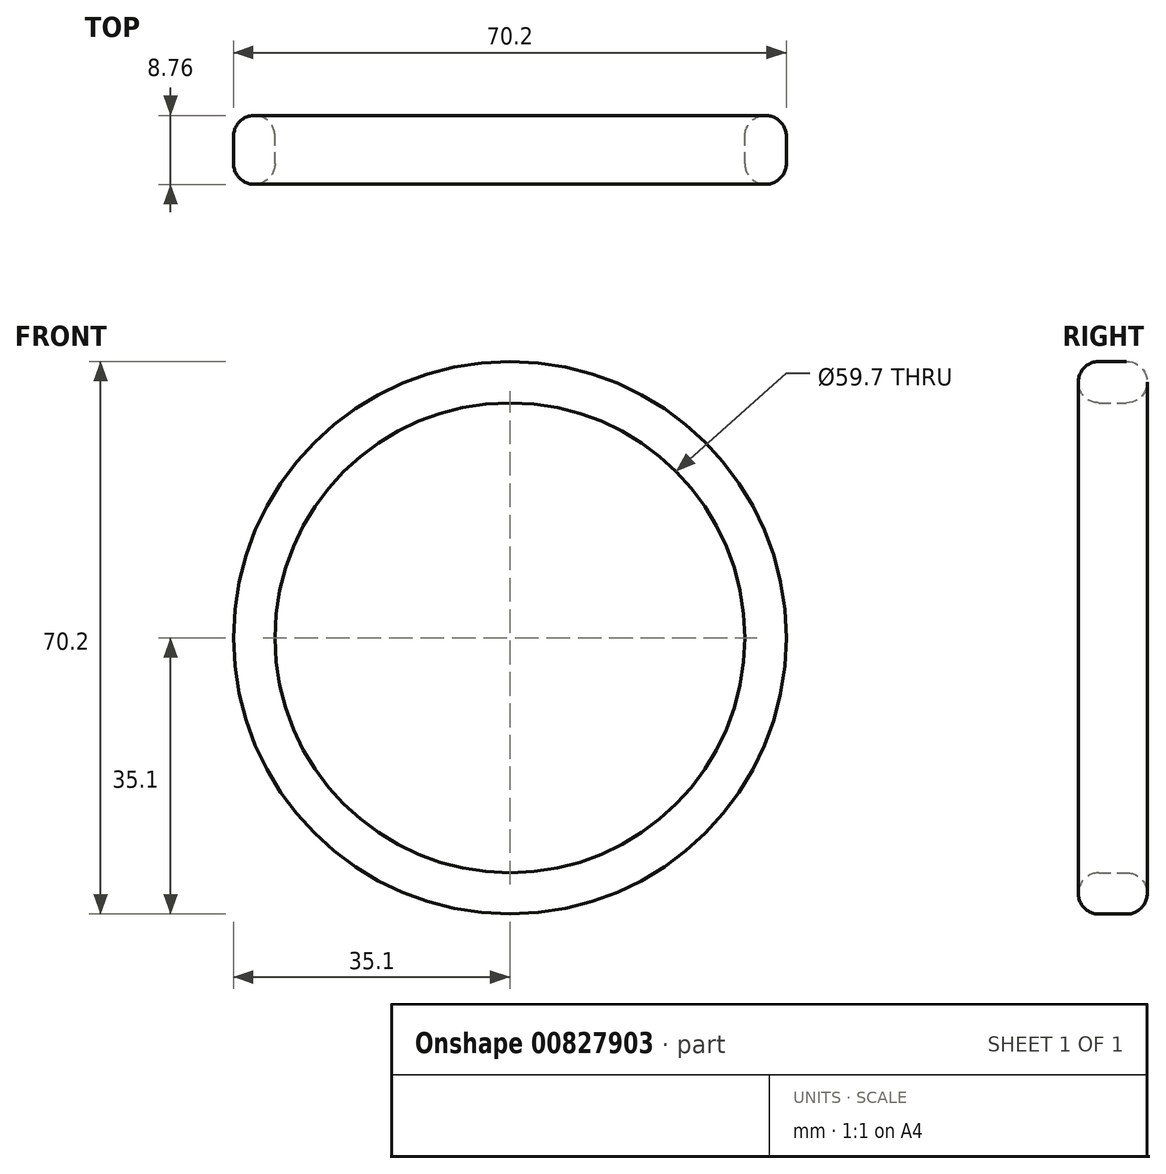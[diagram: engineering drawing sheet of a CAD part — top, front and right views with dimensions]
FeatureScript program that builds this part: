
annotation { "Feature Type Name" : "Feature", "Feature Type Description" : "" }
export const myFeature = defineFeature(function(context is Context, id is Id, definition is map)
    precondition{}
    {
        {
            var Q0;
            Q0=qCreatedBy(makeId("Right.planeOp"),FACE);
            var sketch = newSketch(context, id + "F0", { "sketchPlane" : qUnion([Q0])});
            skLineSegment(sketch, "E0.bottom", {"start": v(1.75, 35.1) * mm, "end": v(-1.75, 35.1) * mm});
            skLineSegment(sketch, "E0.top", {"start": v(1.75, 29.85) * mm, "end": v(-1.75, 29.85) * mm});
            skPoint(sketch, "E0.middle", {"position": v(0, 32.48) * mm});
            skArc(sketch, "E1", {"start": v(1.75, 29.85) * mm, "mid": v(4.38, 32.48) * mm, "end": v(1.75, 35.1) * mm});
            skArc(sketch, "E2", {"start": v(-1.75, 35.1) * mm, "mid": v(-4.38, 32.48) * mm, "end": v(-1.75, 29.85) * mm});
            skLineSegment(sketch, "E3", {"start": v(0, 0) * mm, "end": v(-9.37, 0) * mm, "construction": true});
            skLineSegment(sketch, "E4", {"start": v(-4.38, 32.48) * mm, "end": v(4.37, 32.48) * mm, "construction": true});
            skSolve(sketch);
        }
        {
            var Q0;
            Q0 = qSketchRegion(id + "F0", true);
            var Q1;
            Q1=sQuery(id+"F0.wireOp",EDGE,"E3");
            revolve(context, id + "F1", {"surfaceOperationType" : NewSurfaceOperationType.NEW, "entities" : qUnion([Q0]), "axis" : qUnion([Q1]), "revolveType" : RevolveType.FULL});
        }
        {
            var Q0;
            Q0=qCreatedBy(makeId("Right.planeOp"),FACE);
            var sketch = newSketch(context, id + "F2", { "sketchPlane" : qUnion([Q0])});
            skLineSegment(sketch, "E5", {"start": v(0.72, 0) * mm, "end": v(-12.76, 0) * mm, "construction": true});
            skArc(sketch, "E6", {"start": v(1.75, 29.85) * mm, "mid": v(3.5, 30.51) * mm, "end": v(4.36, 32.17) * mm});
            skArc(sketch, "E7", {"start": v(4.38, -32.48) * mm, "mid": v(3.6, -30.62) * mm, "end": v(1.75, -29.85) * mm});
            skArc(sketch, "E8", {"start": v(-4.38, 32.48) * mm, "mid": v(-3.6, 30.62) * mm, "end": v(-1.75, 29.85) * mm});
            skLineSegment(sketch, "E9", {"start": v(-1.75, 29.85) * mm, "end": v(1.75, 29.85) * mm});
            skLineSegment(sketch, "E10", {"start": v(-4.38, 32.48) * mm, "end": v(-4.38, -32.48) * mm, "construction": true});
            skLineSegment(sketch, "E11", {"start": v(4.38, 32.48) * mm, "end": v(4.38, -32.48) * mm, "construction": true});
            skLineSegment(sketch, "E12", {"start": v(-4.38, 32.48) * mm, "end": v(-4.38, 27.17) * mm});
            skLineSegment(sketch, "E13", {"start": v(-4.38, 27.17) * mm, "end": v(4.38, 27.17) * mm});
            skLineSegment(sketch, "E14", {"start": v(4.37, 27.17) * mm, "end": v(4.36, 32.17) * mm});
            skSolve(sketch);
        }
        {
            var Q0;
            Q0 = qSketchRegion(id + "F2", true);
            var Q1;
            Q1=sQuery(id+"F2.wireOp",EDGE,"E5");
            revolve(context, id + "F3", {"surfaceOperationType" : NewSurfaceOperationType.NEW, "entities" : qUnion([Q0]), "axis" : qUnion([Q1]), "revolveType" : RevolveType.FULL});
        }
        {
            var Q0;
            Q0=qCreatedBy(makeId("Front.planeOp"),FACE);
            var sketch = newSketch(context, id + "F4", { "sketchPlane" : qUnion([Q0])});
            skArc(sketch, "E15", {"start": v(-1.28, 1.5) * mm, "mid": v(-1.95, -0.29) * mm, "end": v(-0.8, -1.8) * mm});
            skLineSegment(sketch, "E16", {"start": v(-1.28, 1.5) * mm, "end": v(1.28, 1.5) * mm});
            skArc(sketch, "E17", {"start": v(0.8, -6.95) * mm, "mid": v(2.41, -6.57) * mm, "end": v(3.89, -5.82) * mm});
            skLineSegment(sketch, "E18", {"start": v(-0.8, -1.8) * mm, "end": v(-0.8, -6.95) * mm});
            skLineSegment(sketch, "E19", {"start": v(-0.8, -1.8) * mm, "end": v(0.8, -1.8) * mm, "construction": true});
            skLineSegment(sketch, "E20", {"start": v(0.8, -1.8) * mm, "end": v(0.8, -6.95) * mm});
            skArc(sketch, "E21.trimOffspring", {"start": v(0.8, -1.8) * mm, "mid": v(1.95, -0.29) * mm, "end": v(1.28, 1.5) * mm});
            skCircle(sketch, "E22.0", {"center": v(0, 0) * mm, "radius": 27.17 * mm, "construction": true});
            skLineSegment(sketch, "E23", {"start": v(0, 0) * mm, "end": v(13.58, 23.53) * mm, "construction": true});
            skLineSegment(sketch, "E24", {"start": v(13.58, 23.53) * mm, "end": v(-13.58, 23.53) * mm, "construction": true});
            skLineSegment(sketch, "E25", {"start": v(-13.58, 23.53) * mm, "end": v(0, 0) * mm, "construction": true});
            skArc(sketch, "E26", {"start": v(-3.5, 6.06) * mm, "mid": v(-3.3, 6.18) * mm, "end": v(-3.11, 6.3) * mm});
            skArc(sketch, "E27", {"start": v(3.1, 6.28) * mm, "mid": v(8.8, 14.9) * mm, "end": v(10.36, 25.11) * mm});
            skArc(sketch, "E28", {"start": v(3.5, 6.06) * mm, "mid": v(3.3, 6.18) * mm, "end": v(3.11, 6.3) * mm});
            skArc(sketch, "E29", {"start": v(-3.1, 6.28) * mm, "mid": v(-8.8, 14.9) * mm, "end": v(-10.36, 25.11) * mm});
            skArc(sketch, "E30", {"start": v(6.38, 26.4) * mm, "mid": v(8.4, 25.84) * mm, "end": v(10.36, 25.11) * mm});
            skArc(sketch, "E31", {"start": v(-6.38, 26.4) * mm, "mid": v(-8.4, 25.84) * mm, "end": v(-10.36, 25.11) * mm});
            skArc(sketch, "E32.1.0", {"start": v(-7, 0) * mm, "mid": v(-7, -0.22) * mm, "end": v(-7, -0.45) * mm});
            skArc(sketch, "E32.1.1", {"start": v(-3.89, -5.82) * mm, "mid": v(-8.5, -15.08) * mm, "end": v(-16.57, -21.53) * mm});
            skArc(sketch, "E32.1.2", {"start": v(-3.5, -6.06) * mm, "mid": v(-3.7, -5.95) * mm, "end": v(-3.9, -5.84) * mm});
            skArc(sketch, "E32.1.3", {"start": v(-6.99, -0.45) * mm, "mid": v(-17.3, 0.18) * mm, "end": v(-26.93, -3.58) * mm});
            skArc(sketch, "E32.1.4", {"start": v(-19.68, -18.73) * mm, "mid": v(-18.18, -20.2) * mm, "end": v(-16.57, -21.53) * mm});
            skArc(sketch, "E32.1.5", {"start": v(-26.06, -7.68) * mm, "mid": v(-26.57, -5.65) * mm, "end": v(-26.93, -3.58) * mm});
            skArc(sketch, "E32.2.0", {"start": v(3.5, -6.06) * mm, "mid": v(3.7, -5.95) * mm, "end": v(3.9, -5.84) * mm});
            skArc(sketch, "E32.2.1", {"start": v(6.99, -0.45) * mm, "mid": v(17.3, 0.18) * mm, "end": v(26.93, -3.58) * mm});
            skArc(sketch, "E32.2.2", {"start": v(7, 0) * mm, "mid": v(7, -0.22) * mm, "end": v(7, -0.45) * mm});
            skArc(sketch, "E32.2.3", {"start": v(3.89, -5.82) * mm, "mid": v(8.5, -15.08) * mm, "end": v(16.57, -21.53) * mm});
            skArc(sketch, "E32.2.4", {"start": v(26.06, -7.68) * mm, "mid": v(26.57, -5.65) * mm, "end": v(26.93, -3.58) * mm});
            skArc(sketch, "E32.2.5", {"start": v(19.68, -18.73) * mm, "mid": v(18.18, -20.2) * mm, "end": v(16.57, -21.53) * mm});
            skArc(sketch, "E33.trimOffspring", {"start": v(0, 8.62) * mm, "mid": v(5.4, 16.72) * mm, "end": v(6.38, 26.4) * mm});
            skArc(sketch, "E34.trimOffspring", {"start": v(0, 8.62) * mm, "mid": v(-5.4, 16.72) * mm, "end": v(-6.38, 26.4) * mm});
            skArc(sketch, "E35.trimOffspring", {"start": v(7.47, -4.31) * mm, "mid": v(11.78, -13.04) * mm, "end": v(19.68, -18.73) * mm});
            skArc(sketch, "E36.trimOffspring", {"start": v(7.47, -4.31) * mm, "mid": v(17.18, -3.68) * mm, "end": v(26.06, -7.68) * mm});
            skArc(sketch, "E37.trimOffspring", {"start": v(6.99, -0.45) * mm, "mid": v(6.06, 3.5) * mm, "end": v(3.1, 6.28) * mm});
            skArc(sketch, "E38.trimOffspring", {"start": v(-3.1, 6.28) * mm, "mid": v(-6.06, 3.5) * mm, "end": v(-6.99, -0.45) * mm});
            skArc(sketch, "E39.trimOffspring", {"start": v(-7.47, -4.31) * mm, "mid": v(-11.78, -13.04) * mm, "end": v(-19.68, -18.73) * mm});
            skArc(sketch, "E40.trimOffspring", {"start": v(-7.47, -4.31) * mm, "mid": v(-17.18, -3.68) * mm, "end": v(-26.06, -7.68) * mm});
            skArc(sketch, "E41.trimOffspring", {"start": v(-3.89, -5.82) * mm, "mid": v(-2.41, -6.57) * mm, "end": v(-0.8, -6.95) * mm});
            skSolve(sketch);
        }
        {
            var Q0;
            Q0=makeQuery(id+"F4.imprint","IMPRINT",FACE,{"disambiguationData":[TD([[makeQuery(id+"F4.imprint","IMPRINT",EDGE,{"derivedFrom":sQuery(id+"F4.wireOp",EDGE,"E15")}),-1.0]])]});
            extrude(context, id + "F5", {"entities" : qUnion([Q0]), "operationType" : NewBodyOperationType.ADD, "endBound" : BoundingType.SYMMETRIC, "depth" : 12 * mm, "offsetDistance" : 25 * mm});
        }
        {
            var Q0;
            Q0=qCreatedBy(makeId("Right.planeOp"),FACE);
            var sketch = newSketch(context, id + "F6", { "sketchPlane" : qUnion([Q0])});
            skPoint(sketch, "E42.0", {"position": v(0, 0) * mm});
            skPoint(sketch, "E43", {"position": v(6, 4) * mm});
            skPoint(sketch, "E44.0", {"position": v(-4.38, 27.17) * mm});
            skPoint(sketch, "E45.0", {"position": v(4.38, 27.17) * mm});
            skPoint(sketch, "E46", {"position": v(-6, 4) * mm});
            skArc(sketch, "E47", {"start": v(-6, 4) * mm, "mid": v(-1.88, 15.35) * mm, "end": v(-4.37, 27.17) * mm});
            skArc(sketch, "E48", {"start": v(4.38, 27.17) * mm, "mid": v(1.88, 15.35) * mm, "end": v(6, 4) * mm});
            skLineSegment(sketch, "E49", {"start": v(-4.38, 27.17) * mm, "end": v(-11.73, 27.17) * mm});
            skLineSegment(sketch, "E50", {"start": v(-11.73, 27.17) * mm, "end": v(-13.05, 2.7) * mm});
            skLineSegment(sketch, "E51", {"start": v(-13.05, 2.7) * mm, "end": v(-6, 4) * mm});
            skLineSegment(sketch, "E52", {"start": v(4.37, 27.17) * mm, "end": v(12.88, 27.73) * mm});
            skLineSegment(sketch, "E53", {"start": v(12.88, 27.73) * mm, "end": v(14.36, 5.35) * mm});
            skLineSegment(sketch, "E54", {"start": v(14.36, 5.35) * mm, "end": v(6, 4) * mm});
            skLineSegment(sketch, "E55", {"start": v(-28.3, 0) * mm, "end": v(18.38, 0) * mm, "construction": true});
            skSolve(sketch);
        }
        {
            var Q0;
            Q0 = qSketchRegion(id + "F6", true);
            var Q1;
            Q1=sQuery(id+"F6.wireOp",EDGE,"E55");
            revolve(context, id + "F7", {"operationType" : NewBodyOperationType.REMOVE, "surfaceOperationType" : NewSurfaceOperationType.NEW, "entities" : qUnion([Q0]), "axis" : qUnion([Q1]), "revolveType" : RevolveType.FULL, "oppositeDirection" : true});
        }
        {
            var Q0;
            {var subQ0=sQuery(id+"F4.wireOp",EDGE,"E33.trimOffspring");Q0=makeQuery(id+"F5.boolean.opBoolean","SPLIT",EDGE,{"disambiguationData":[topologyDisambiguationEdgeConnected([makeQuery(id+"F3.opRevolve","SWEPT_FACE",FACE,{"disambiguationData":[OSD([sQuery(id+"F2.wireOp",EDGE,"E13")])]}),makeQuery(id+"F5.opExtrude","SWEPT_FACE",FACE,{"disambiguationData":[OSD([subQ0])]})])],"derivedFrom":makeQuery(id+"F5.opExtrude","SWEPT_EDGE",EDGE,{"disambiguationData":[OSD([sQuery(id+"F4.wireOp",EDGE,"E30"),subQ0])]})});}
            var Q1;
            {var subQ0=sQuery(id+"F4.wireOp",EDGE,"E36.trimOffspring");Q1=makeQuery(id+"F5.boolean.opBoolean","SPLIT",EDGE,{"disambiguationData":[topologyDisambiguationEdgeConnected([makeQuery(id+"F3.opRevolve","SWEPT_FACE",FACE,{"disambiguationData":[OSD([sQuery(id+"F2.wireOp",EDGE,"E13")])]}),makeQuery(id+"F5.opExtrude","SWEPT_FACE",FACE,{"disambiguationData":[OSD([subQ0])]})])],"derivedFrom":makeQuery(id+"F5.opExtrude","SWEPT_EDGE",EDGE,{"disambiguationData":[OSD([sQuery(id+"F4.wireOp",EDGE,"E32.2.4"),subQ0])]})});}
            var Q2;
            {var subQ0=sQuery(id+"F4.wireOp",EDGE,"E32.2.3");Q2=makeQuery(id+"F5.boolean.opBoolean","SPLIT",EDGE,{"disambiguationData":[topologyDisambiguationEdgeConnected([makeQuery(id+"F3.opRevolve","SWEPT_FACE",FACE,{"disambiguationData":[OSD([sQuery(id+"F2.wireOp",EDGE,"E13")])]}),makeQuery(id+"F5.opExtrude","SWEPT_FACE",FACE,{"disambiguationData":[OSD([subQ0])]})])],"derivedFrom":makeQuery(id+"F5.opExtrude","SWEPT_EDGE",EDGE,{"disambiguationData":[OSD([subQ0,sQuery(id+"F4.wireOp",EDGE,"E32.2.5")])]})});}
            var Q3;
            Q3=makeQuery(id+"F5.opExtrude","SWEPT_EDGE",EDGE,{"disambiguationData":[OSD([sQuery(id+"F4.wireOp",EDGE,"E39.trimOffspring"),sQuery(id+"F4.wireOp",EDGE,"E40.trimOffspring")])]});
            var Q4;
            Q4=makeQuery(id+"F5.opExtrude","SWEPT_EDGE",EDGE,{"disambiguationData":[OSD([sQuery(id+"F4.wireOp",EDGE,"E29"),sQuery(id+"F4.wireOp",EDGE,"E38.trimOffspring")])]});
            var Q5;
            {var subQ0=sQuery(id+"F4.wireOp",EDGE,"E34.trimOffspring");Q5=makeQuery(id+"F5.boolean.opBoolean","SPLIT",EDGE,{"disambiguationData":[topologyDisambiguationEdgeConnected([makeQuery(id+"F3.opRevolve","SWEPT_FACE",FACE,{"disambiguationData":[OSD([sQuery(id+"F2.wireOp",EDGE,"E13")])]}),makeQuery(id+"F5.opExtrude","SWEPT_FACE",FACE,{"disambiguationData":[OSD([subQ0])]})])],"derivedFrom":makeQuery(id+"F5.opExtrude","SWEPT_EDGE",EDGE,{"disambiguationData":[OSD([sQuery(id+"F4.wireOp",EDGE,"E31"),subQ0])]})});}
            var Q6;
            {var subQ0=sQuery(id+"F4.wireOp",EDGE,"E40.trimOffspring");Q6=makeQuery(id+"F5.boolean.opBoolean","SPLIT",EDGE,{"disambiguationData":[topologyDisambiguationEdgeConnected([makeQuery(id+"F3.opRevolve","SWEPT_FACE",FACE,{"disambiguationData":[OSD([sQuery(id+"F2.wireOp",EDGE,"E13")])]}),makeQuery(id+"F5.opExtrude","SWEPT_FACE",FACE,{"disambiguationData":[OSD([subQ0])]})])],"derivedFrom":makeQuery(id+"F5.opExtrude","SWEPT_EDGE",EDGE,{"disambiguationData":[OSD([sQuery(id+"F4.wireOp",EDGE,"E32.1.5"),subQ0])]})});}
            var Q7;
            {var subQ0=sQuery(id+"F4.wireOp",EDGE,"E32.1.1");Q7=makeQuery(id+"F5.boolean.opBoolean","SPLIT",EDGE,{"disambiguationData":[topologyDisambiguationEdgeConnected([makeQuery(id+"F3.opRevolve","SWEPT_FACE",FACE,{"disambiguationData":[OSD([sQuery(id+"F2.wireOp",EDGE,"E13")])]}),makeQuery(id+"F5.opExtrude","SWEPT_FACE",FACE,{"disambiguationData":[OSD([subQ0])]})])],"derivedFrom":makeQuery(id+"F5.opExtrude","SWEPT_EDGE",EDGE,{"disambiguationData":[OSD([subQ0,sQuery(id+"F4.wireOp",EDGE,"E32.1.4")])]})});}
            var Q8;
            Q8=makeQuery(id+"F5.opExtrude","SWEPT_EDGE",EDGE,{"disambiguationData":[OSD([sQuery(id+"F4.wireOp",EDGE,"E35.trimOffspring"),sQuery(id+"F4.wireOp",EDGE,"E36.trimOffspring")])]});
            var Q9;
            Q9=makeQuery(id+"F5.opExtrude","SWEPT_EDGE",EDGE,{"disambiguationData":[OSD([sQuery(id+"F4.wireOp",EDGE,"E32.2.1"),sQuery(id+"F4.wireOp",EDGE,"E37.trimOffspring")])]});
            var Q10;
            Q10=makeQuery(id+"F5.opExtrude","SWEPT_EDGE",EDGE,{"disambiguationData":[OSD([sQuery(id+"F4.wireOp",EDGE,"E33.trimOffspring"),sQuery(id+"F4.wireOp",EDGE,"E34.trimOffspring")])]});
            var Q11;
            {var subQ0=sQuery(id+"F4.wireOp",EDGE,"E39.trimOffspring");Q11=makeQuery(id+"F5.boolean.opBoolean","SPLIT",EDGE,{"disambiguationData":[topologyDisambiguationEdgeConnected([makeQuery(id+"F3.opRevolve","SWEPT_FACE",FACE,{"disambiguationData":[OSD([sQuery(id+"F2.wireOp",EDGE,"E13")])]}),makeQuery(id+"F5.opExtrude","SWEPT_FACE",FACE,{"disambiguationData":[OSD([subQ0])]})])],"derivedFrom":makeQuery(id+"F5.opExtrude","SWEPT_EDGE",EDGE,{"disambiguationData":[OSD([sQuery(id+"F4.wireOp",EDGE,"E32.1.4"),subQ0])]})});}
            var Q12;
            {var subQ0=sQuery(id+"F4.wireOp",EDGE,"E32.1.3");Q12=makeQuery(id+"F5.boolean.opBoolean","SPLIT",EDGE,{"disambiguationData":[topologyDisambiguationEdgeConnected([makeQuery(id+"F3.opRevolve","SWEPT_FACE",FACE,{"disambiguationData":[OSD([sQuery(id+"F2.wireOp",EDGE,"E13")])]}),makeQuery(id+"F5.opExtrude","SWEPT_FACE",FACE,{"disambiguationData":[OSD([subQ0])]})])],"derivedFrom":makeQuery(id+"F5.opExtrude","SWEPT_EDGE",EDGE,{"disambiguationData":[OSD([subQ0,sQuery(id+"F4.wireOp",EDGE,"E32.1.5")])]})});}
            var Q13;
            Q13=makeQuery(id+"F5.opExtrude","SWEPT_EDGE",EDGE,{"disambiguationData":[OSD([sQuery(id+"F4.wireOp",EDGE,"E32.1.3"),sQuery(id+"F4.wireOp",EDGE,"E38.trimOffspring")])]});
            var Q14;
            {var subQ0=sQuery(id+"F4.wireOp",EDGE,"E35.trimOffspring");Q14=makeQuery(id+"F5.boolean.opBoolean","SPLIT",EDGE,{"disambiguationData":[topologyDisambiguationEdgeConnected([makeQuery(id+"F3.opRevolve","SWEPT_FACE",FACE,{"disambiguationData":[OSD([sQuery(id+"F2.wireOp",EDGE,"E13")])]}),makeQuery(id+"F5.opExtrude","SWEPT_FACE",FACE,{"disambiguationData":[OSD([subQ0])]})])],"derivedFrom":makeQuery(id+"F5.opExtrude","SWEPT_EDGE",EDGE,{"disambiguationData":[OSD([sQuery(id+"F4.wireOp",EDGE,"E32.2.5"),subQ0])]})});}
            var Q15;
            {var subQ0=sQuery(id+"F4.wireOp",EDGE,"E32.2.1");Q15=makeQuery(id+"F5.boolean.opBoolean","SPLIT",EDGE,{"disambiguationData":[topologyDisambiguationEdgeConnected([makeQuery(id+"F3.opRevolve","SWEPT_FACE",FACE,{"disambiguationData":[OSD([sQuery(id+"F2.wireOp",EDGE,"E13")])]}),makeQuery(id+"F5.opExtrude","SWEPT_FACE",FACE,{"disambiguationData":[OSD([subQ0])]})])],"derivedFrom":makeQuery(id+"F5.opExtrude","SWEPT_EDGE",EDGE,{"disambiguationData":[OSD([subQ0,sQuery(id+"F4.wireOp",EDGE,"E32.2.4")])]})});}
            var Q16;
            Q16=makeQuery(id+"F5.opExtrude","SWEPT_EDGE",EDGE,{"disambiguationData":[OSD([sQuery(id+"F4.wireOp",EDGE,"E27"),sQuery(id+"F4.wireOp",EDGE,"E37.trimOffspring")])]});
            var Q17;
            {var subQ0=sQuery(id+"F4.wireOp",EDGE,"E29");Q17=makeQuery(id+"F5.boolean.opBoolean","SPLIT",EDGE,{"disambiguationData":[topologyDisambiguationEdgeConnected([makeQuery(id+"F3.opRevolve","SWEPT_FACE",FACE,{"disambiguationData":[OSD([sQuery(id+"F2.wireOp",EDGE,"E13")])]}),makeQuery(id+"F5.opExtrude","SWEPT_FACE",FACE,{"disambiguationData":[OSD([subQ0])]})])],"derivedFrom":makeQuery(id+"F5.opExtrude","SWEPT_EDGE",EDGE,{"disambiguationData":[OSD([subQ0,sQuery(id+"F4.wireOp",EDGE,"E31")])]})});}
            var Q18;
            {var subQ0=sQuery(id+"F4.wireOp",EDGE,"E27");Q18=makeQuery(id+"F5.boolean.opBoolean","SPLIT",EDGE,{"disambiguationData":[topologyDisambiguationEdgeConnected([makeQuery(id+"F3.opRevolve","SWEPT_FACE",FACE,{"disambiguationData":[OSD([sQuery(id+"F2.wireOp",EDGE,"E13")])]}),makeQuery(id+"F5.opExtrude","SWEPT_FACE",FACE,{"disambiguationData":[OSD([subQ0])]})])],"derivedFrom":makeQuery(id+"F5.opExtrude","SWEPT_EDGE",EDGE,{"disambiguationData":[OSD([subQ0,sQuery(id+"F4.wireOp",EDGE,"E30")])]})});}
            var Q19;
            Q19=makeQuery(id+"F5.opExtrude","SWEPT_EDGE",EDGE,{"disambiguationData":[OSD([sQuery(id+"F4.wireOp",EDGE,"E18"),sQuery(id+"F4.wireOp",EDGE,"E41.trimOffspring")])]});
            var Q20;
            Q20=makeQuery(id+"F5.opExtrude","SWEPT_EDGE",EDGE,{"disambiguationData":[OSD([sQuery(id+"F4.wireOp",EDGE,"E32.1.1"),sQuery(id+"F4.wireOp",EDGE,"E41.trimOffspring")])]});
            var Q21;
            Q21=makeQuery(id+"F5.opExtrude","SWEPT_EDGE",EDGE,{"disambiguationData":[OSD([sQuery(id+"F4.wireOp",EDGE,"E17"),sQuery(id+"F4.wireOp",EDGE,"E32.2.3")])]});
            var Q22;
            Q22=makeQuery(id+"F5.opExtrude","SWEPT_EDGE",EDGE,{"disambiguationData":[OSD([sQuery(id+"F4.wireOp",EDGE,"E17"),sQuery(id+"F4.wireOp",EDGE,"E20")])]});
            var Q23;
            Q23=makeQuery(id+"F5.opExtrude","SWEPT_EDGE",EDGE,{"disambiguationData":[OSD([sQuery(id+"F4.wireOp",EDGE,"E15"),sQuery(id+"F4.wireOp",EDGE,"E18")])]});
            var Q24;
            Q24=makeQuery(id+"F5.opExtrude","SWEPT_EDGE",EDGE,{"disambiguationData":[OSD([sQuery(id+"F4.wireOp",EDGE,"E20"),sQuery(id+"F4.wireOp",EDGE,"E21.trimOffspring")])]});
            fillet(context, id + "F8", {"entities" : qUnion([Q0, Q1, Q2, Q3, Q4, Q5, Q6, Q7, Q8, Q9, Q10, Q11, Q12, Q13, Q14, Q15, Q16, Q17, Q18, Q19, Q20, Q21, Q22, Q23, Q24]), "radius" : 1 * mm, "tangentPropagation" : true, "allowEdgeOverflow" : false});
        }
        {
            var Q0;
            Q0=makeQuery(id+"F7.boolean.opBoolean","SPLIT",BODY,{"disambiguationData":[OD(1.0)],"derivedFrom":makeQuery(id+"F3.opRevolve","SWEPT_BODY",BODY,{"disambiguationData":[OSD([sQuery(id+"F2.wireOp",EDGE,"E6"),sQuery(id+"F2.wireOp",EDGE,"E8"),sQuery(id+"F2.wireOp",EDGE,"E9"),sQuery(id+"F2.wireOp",EDGE,"E12"),sQuery(id+"F2.wireOp",EDGE,"E13"),sQuery(id+"F2.wireOp",EDGE,"E14")])]})});
            var Q1;
            Q1=makeQuery(id+"F7.boolean.opBoolean","SPLIT",BODY,{"disambiguationData":[OD(2.0)],"derivedFrom":makeQuery(id+"F3.opRevolve","SWEPT_BODY",BODY,{"disambiguationData":[OSD([sQuery(id+"F2.wireOp",EDGE,"E6"),sQuery(id+"F2.wireOp",EDGE,"E8"),sQuery(id+"F2.wireOp",EDGE,"E9"),sQuery(id+"F2.wireOp",EDGE,"E12"),sQuery(id+"F2.wireOp",EDGE,"E13"),sQuery(id+"F2.wireOp",EDGE,"E14")])]})});
            var Q2;
            Q2=makeQuery(id+"F7.boolean.opBoolean","SPLIT",BODY,{"disambiguationData":[OD(3.0)],"derivedFrom":makeQuery(id+"F3.opRevolve","SWEPT_BODY",BODY,{"disambiguationData":[OSD([sQuery(id+"F2.wireOp",EDGE,"E6"),sQuery(id+"F2.wireOp",EDGE,"E8"),sQuery(id+"F2.wireOp",EDGE,"E9"),sQuery(id+"F2.wireOp",EDGE,"E12"),sQuery(id+"F2.wireOp",EDGE,"E13"),sQuery(id+"F2.wireOp",EDGE,"E14")])]})});
            var Q3;
            Q3=makeQuery(id+"F7.boolean.opBoolean","SPLIT",BODY,{"disambiguationData":[OD(4.0)],"derivedFrom":makeQuery(id+"F3.opRevolve","SWEPT_BODY",BODY,{"disambiguationData":[OSD([sQuery(id+"F2.wireOp",EDGE,"E6"),sQuery(id+"F2.wireOp",EDGE,"E8"),sQuery(id+"F2.wireOp",EDGE,"E9"),sQuery(id+"F2.wireOp",EDGE,"E12"),sQuery(id+"F2.wireOp",EDGE,"E13"),sQuery(id+"F2.wireOp",EDGE,"E14")])]})});
            var Q4;
            Q4=makeQuery(id+"F7.boolean.opBoolean","SPLIT",BODY,{"disambiguationData":[OD(5.0)],"derivedFrom":makeQuery(id+"F3.opRevolve","SWEPT_BODY",BODY,{"disambiguationData":[OSD([sQuery(id+"F2.wireOp",EDGE,"E6"),sQuery(id+"F2.wireOp",EDGE,"E8"),sQuery(id+"F2.wireOp",EDGE,"E9"),sQuery(id+"F2.wireOp",EDGE,"E12"),sQuery(id+"F2.wireOp",EDGE,"E13"),sQuery(id+"F2.wireOp",EDGE,"E14")])]})});
            var Q5;
            Q5=makeQuery(id+"F7.boolean.opBoolean","SPLIT",BODY,{"disambiguationData":[OD(6.0)],"derivedFrom":makeQuery(id+"F3.opRevolve","SWEPT_BODY",BODY,{"disambiguationData":[OSD([sQuery(id+"F2.wireOp",EDGE,"E6"),sQuery(id+"F2.wireOp",EDGE,"E8"),sQuery(id+"F2.wireOp",EDGE,"E9"),sQuery(id+"F2.wireOp",EDGE,"E12"),sQuery(id+"F2.wireOp",EDGE,"E13"),sQuery(id+"F2.wireOp",EDGE,"E14")])]})});
            deleteBodies(context, id + "F9", {"entities" : qUnion([Q0, Q1, Q2, Q3, Q4, Q5])});
        }
    });
